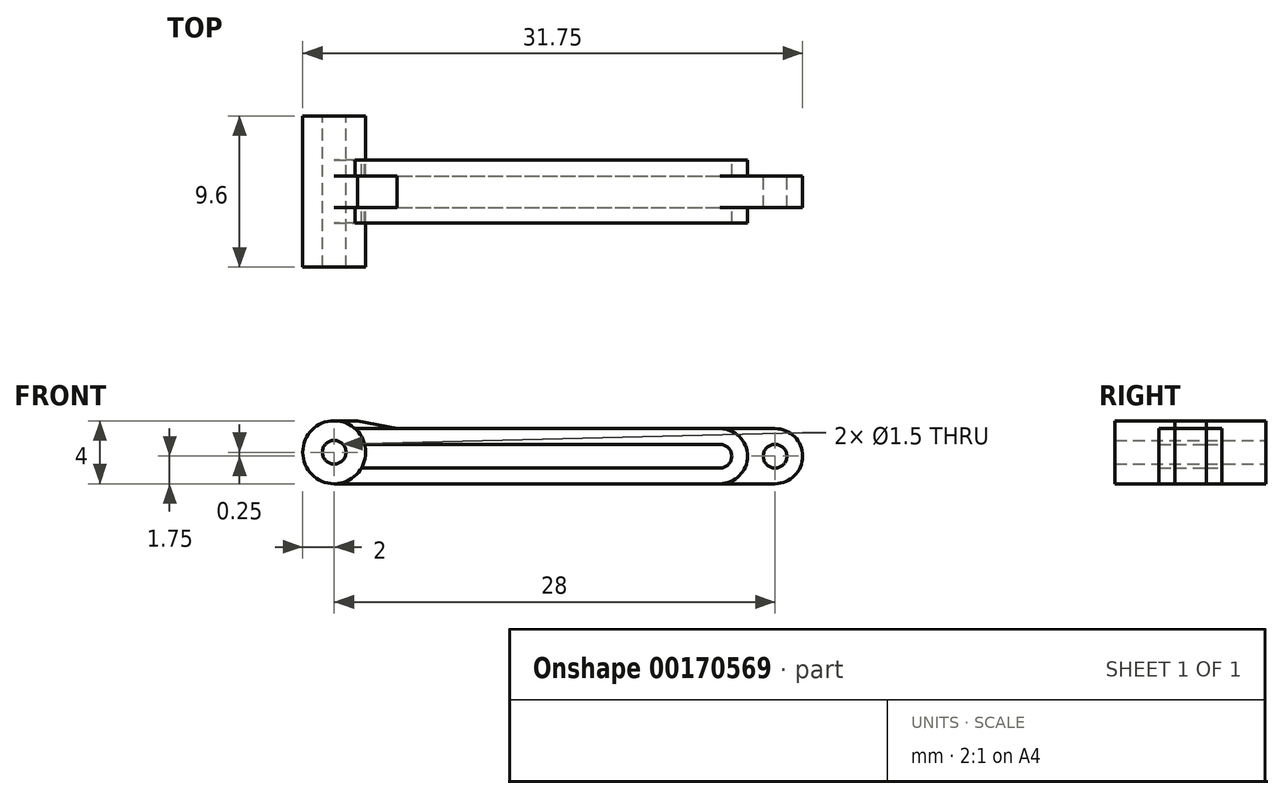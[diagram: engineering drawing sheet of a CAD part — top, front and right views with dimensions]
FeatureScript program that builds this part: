
annotation { "Feature Type Name" : "Feature", "Feature Type Description" : "" }
export const myFeature = defineFeature(function(context is Context, id is Id, definition is map)
    precondition{}
    {
        {
            var Q0;
            Q0=qCreatedBy(makeId("Front.planeOp"),FACE);
            var sketch = newSketch(context, id + "F0", { "sketchPlane" : qUnion([Q0])});
            skLineSegment(sketch, "E0.bottom", {"start": v(0, 0) * mm, "end": v(24, 0) * mm});
            skLineSegment(sketch, "E0.top", {"start": v(0, 3.5) * mm, "end": v(24, 3.5) * mm});
            skLineSegment(sketch, "E0.left", {"start": v(0, 0) * mm, "end": v(0, 3.5) * mm, "construction": true});
            skLineSegment(sketch, "E0.right", {"start": v(24, 0) * mm, "end": v(24, 3.5) * mm, "construction": true});
            skCircle(sketch, "E1", {"center": v(24, 1.75) * mm, "radius": 0.75 * mm});
            skArc(sketch, "E2", {"start": v(24, 3.5) * mm, "mid": v(25.75, 1.75) * mm, "end": v(24, 0) * mm});
            skLineSegment(sketch, "E3", {"start": v(0, 0) * mm, "end": v(-4, 0) * mm});
            skLineSegment(sketch, "E4", {"start": v(-4, 0) * mm, "end": v(-4, 4) * mm, "construction": true});
            skLineSegment(sketch, "E5", {"start": v(-4, 4) * mm, "end": v(-2.5, 4) * mm});
            skLineSegment(sketch, "E6", {"start": v(-2.5, 4) * mm, "end": v(0, 3.5) * mm});
            skCircle(sketch, "E7", {"center": v(-4, 2) * mm, "radius": 0.75 * mm});
            skCircle(sketch, "E8", {"center": v(-4, 2) * mm, "radius": 2 * mm});
            skSolve(sketch);
        }
        {
            var Q0;
            Q0 = qSketchRegion(id + "F0", true);
            extrude(context, id + "F1", {"entities" : qUnion([Q0]), "endBound" : BoundingType.SYMMETRIC, "depth" : 2 * mm});
        }
        {
            var Q0;
            Q0=makeQuery(id+"F0.imprint","IMPRINT",FACE,{"disambiguationData":[TD([[makeQuery(id+"F0.imprint","IMPRINT",EDGE,{"derivedFrom":sQuery(id+"F0.wireOp",EDGE,"E7")}),-1.0]])]});
            extrude(context, id + "F2", {"entities" : qUnion([Q0]), "operationType" : NewBodyOperationType.ADD, "endBound" : BoundingType.SYMMETRIC, "depth" : 9.6 * mm});
        }
        {
            var Q0;
            Q0=qCreatedBy(makeId("Front.planeOp"),FACE);
            var sketch = newSketch(context, id + "F3", { "sketchPlane" : qUnion([Q0])});
            skLineSegment(sketch, "E9.0", {"start": v(0, 3.5) * mm, "end": v(20.5, 3.5) * mm});
            skLineSegment(sketch, "E10.0", {"start": v(20.5, 0) * mm, "end": v(-4, 0) * mm});
            skLineSegment(sketch, "E11.0", {"start": v(0, 2.5) * mm, "end": v(20.5, 2.5) * mm});
            skLineSegment(sketch, "E12.0", {"start": v(20.5, 1) * mm, "end": v(-4, 1) * mm});
            skLineSegment(sketch, "E13", {"start": v(20.5, 2.5) * mm, "end": v(20.5, 1) * mm, "construction": true});
            skArc(sketch, "E14", {"start": v(20.5, 2.5) * mm, "mid": v(21.25, 1.75) * mm, "end": v(20.5, 1) * mm});
            skLineSegment(sketch, "E15", {"start": v(-4, 1) * mm, "end": v(-4, 0) * mm});
            skLineSegment(sketch, "E16", {"start": v(0, 2.5) * mm, "end": v(-3.02, 2.5) * mm});
            skLineSegment(sketch, "E17", {"start": v(-3.02, 2.5) * mm, "end": v(-3.02, 3.5) * mm});
            skLineSegment(sketch, "E18", {"start": v(-3.02, 3.5) * mm, "end": v(0, 3.5) * mm});
            skArc(sketch, "E19", {"start": v(20.5, 3.5) * mm, "mid": v(22.25, 1.75) * mm, "end": v(20.5, 0) * mm});
            skPoint(sketch, "E20.orphan", {"position": v(24, 0) * mm});
            skPoint(sketch, "E21.orphan", {"position": v(24, 3.5) * mm});
            skSolve(sketch);
        }
        {
            var Q0;
            Q0 = qSketchRegion(id + "F3", true);
            extrude(context, id + "F4", {"entities" : qUnion([Q0]), "operationType" : NewBodyOperationType.ADD, "endBound" : BoundingType.SYMMETRIC, "depth" : 4 * mm});
        }
    });
